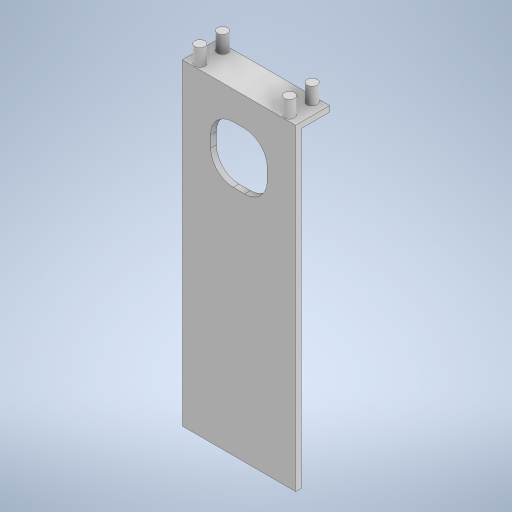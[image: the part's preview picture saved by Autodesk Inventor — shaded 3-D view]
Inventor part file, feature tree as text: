
AUTODESK INVENTOR PART (.ipt)
format: ipt  version: 2023 (Build 270158000, 158)  size: 287,744 bytes
history: native  units: mm
features: extrude x5, sketch x5
ambient origin geometry x8: Origin, YZ Plane, XZ Plane, XY Plane, X Axis, Y Axis, Z Axis, Center Point
bodies: Solid1 (feature_tree)
feature tree (10):
  extrude  "Extrusion1"  Depth=100.0mm
  extrude  "Extrusion6"  Depth=50.0mm
  sketch  "Sketch15"  dims[d22=50.0mm d23=20.0mm]
  sketch  "Sketch16"  dims[d24=5.0mm d25=0.0mm d46=100.0mm]
  extrude  "Extrusion11"  Depth=20.0mm
  extrude  "Extrusion12"  Depth=100.0mm
  extrude  "Extrusion17"  Depth=5.0mm
  sketch  "Sketch1"  dims[d0=100.0mm d1=200.0mm]
  sketch  "Sketch6"  dims[d2=5.0mm d3=0.0mm d21=50.0mm]
  sketch  "Sketch21"  dims[d47=30.0mm d48=9.0mm d49=9.0mm d50=9.0mm d51=9.0mm d52=5.0mm d53=0.0mm d54=15.0mm d55=0.0mm d66=100.0mm d67=80.0mm d68=5.0mm d69=0.0mm]
